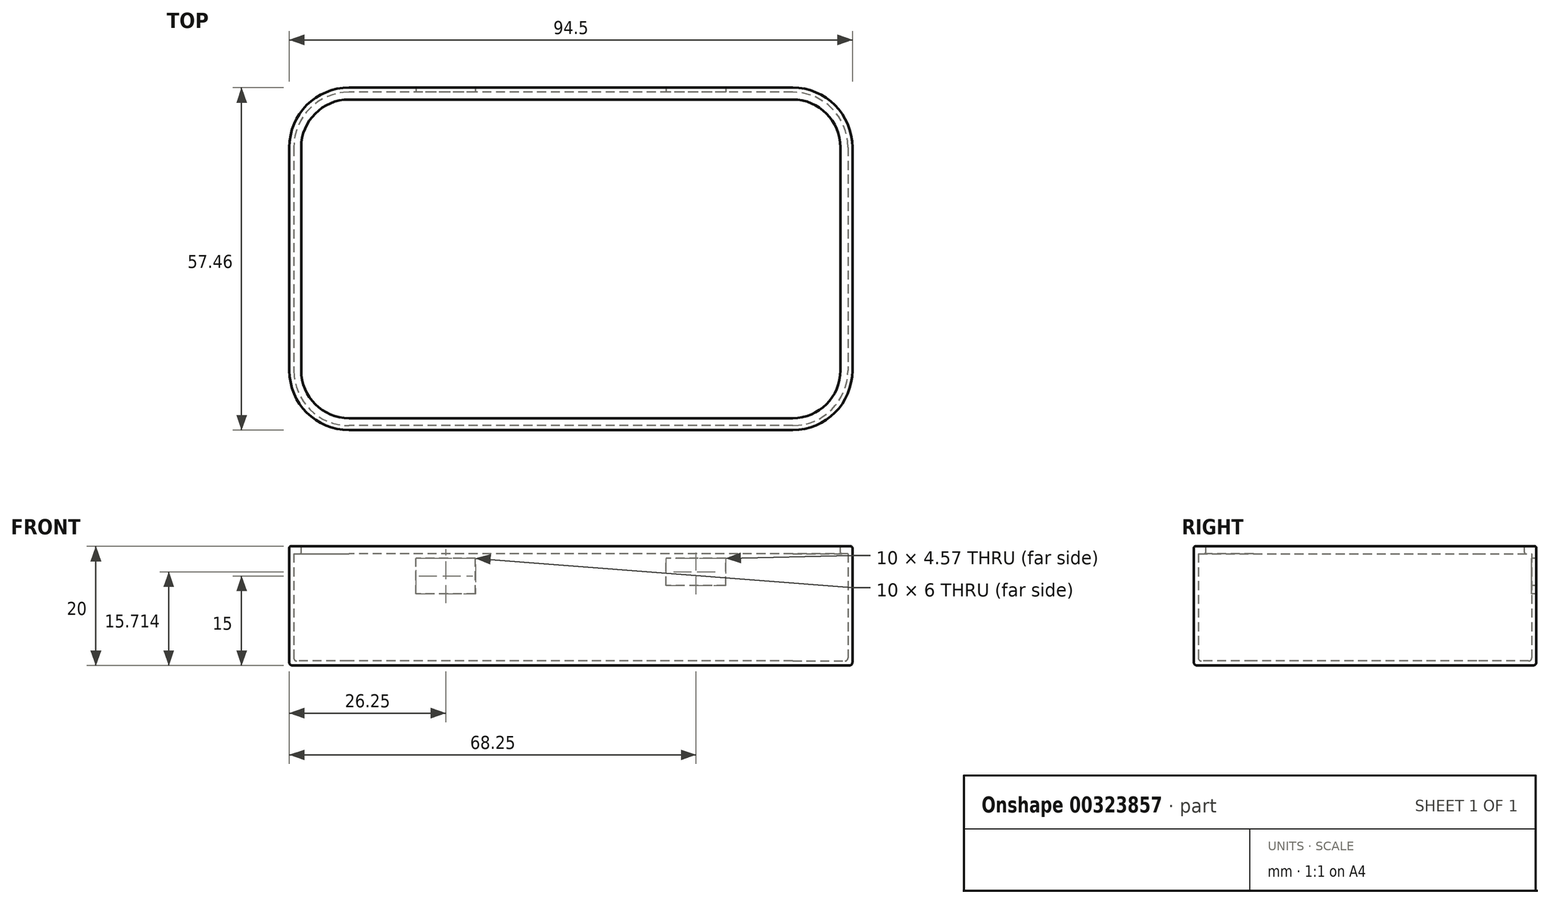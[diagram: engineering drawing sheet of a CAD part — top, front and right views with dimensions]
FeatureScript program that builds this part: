
annotation { "Feature Type Name" : "Feature", "Feature Type Description" : "" }
export const myFeature = defineFeature(function(context is Context, id is Id, definition is map)
    precondition{}
    {
        {
            var Q0;
            Q0=qCreatedBy(makeId("Top.planeOp"),FACE);
            var sketch = newSketch(context, id + "F0", { "sketchPlane" : qUnion([Q0])});
            skLineSegment(sketch, "E0.bottom", {"start": v(37.25, 28.73) * mm, "end": v(-37.25, 28.73) * mm});
            skLineSegment(sketch, "E0.top", {"start": v(37.25, -28.73) * mm, "end": v(-37.25, -28.73) * mm});
            skLineSegment(sketch, "E0.left", {"start": v(47.25, 18.73) * mm, "end": v(47.25, -18.73) * mm});
            skLineSegment(sketch, "E0.right", {"start": v(-47.25, 18.73) * mm, "end": v(-47.25, -18.73) * mm});
            skPoint(sketch, "E0.middle", {"position": v(0, 0) * mm});
            skPoint(sketch, "E1.visualSharp", {"position": v(-47.25, 28.73) * mm});
            skArc(sketch, "E1.filletArc", {"start": v(-37.25, 28.73) * mm, "mid": v(-44.32, 25.8) * mm, "end": v(-47.25, 18.73) * mm});
            skPoint(sketch, "E2.visualSharp", {"position": v(-47.25, -28.73) * mm});
            skArc(sketch, "E2.filletArc", {"start": v(-47.25, -18.73) * mm, "mid": v(-44.32, -25.8) * mm, "end": v(-37.25, -28.73) * mm});
            skPoint(sketch, "E3.visualSharp", {"position": v(47.25, -28.73) * mm});
            skArc(sketch, "E3.filletArc", {"start": v(37.25, -28.73) * mm, "mid": v(44.32, -25.8) * mm, "end": v(47.25, -18.73) * mm});
            skPoint(sketch, "E4.visualSharp", {"position": v(47.25, 28.73) * mm});
            skArc(sketch, "E4.filletArc", {"start": v(47.25, 18.73) * mm, "mid": v(44.32, 25.8) * mm, "end": v(37.25, 28.73) * mm});
            skSolve(sketch);
        }
        {
            var Q0;
            Q0 = qSketchRegion(id + "F0", true);
            extrude(context, id + "F1", {"entities" : qUnion([Q0]), "oppositeDirection" : true, "depth" : 20 * mm});
        }
        {
            var Q0;
            Q0=qCreatedBy(makeId("Top.planeOp"),FACE);
            var sketch = newSketch(context, id + "F2", { "sketchPlane" : qUnion([Q0])});
            skArc(sketch, "E5.0", {"start": v(-45.25, -18.73) * mm, "mid": v(-42.9, -24.38) * mm, "end": v(-37.25, -26.73) * mm});
            skLineSegment(sketch, "E5.1", {"start": v(-45.25, 18.73) * mm, "end": v(-45.25, -18.73) * mm});
            skLineSegment(sketch, "E5.2", {"start": v(-37.25, -26.73) * mm, "end": v(37.25, -26.73) * mm});
            skArc(sketch, "E5.3", {"start": v(-37.25, 26.73) * mm, "mid": v(-42.9, 24.38) * mm, "end": v(-45.25, 18.73) * mm});
            skArc(sketch, "E5.4", {"start": v(37.25, -26.73) * mm, "mid": v(42.9, -24.38) * mm, "end": v(45.25, -18.73) * mm});
            skLineSegment(sketch, "E5.5", {"start": v(45.25, -18.73) * mm, "end": v(45.25, 18.73) * mm});
            skArc(sketch, "E5.6", {"start": v(45.25, 18.73) * mm, "mid": v(42.9, 24.38) * mm, "end": v(37.25, 26.73) * mm});
            skLineSegment(sketch, "E5.7", {"start": v(37.25, 26.73) * mm, "end": v(-37.25, 26.73) * mm});
            skSolve(sketch);
        }
        {
            var Q0;
            Q0 = qSketchRegion(id + "F2", true);
            extrude(context, id + "F3", {"entities" : qUnion([Q0]), "operationType" : NewBodyOperationType.REMOVE, "oppositeDirection" : true, "depth" : 19.25 * mm});
        }
        {
            var Q0;
            Q0=makeQuery(id+"F3.boolean.opBoolean","COPY",FACE,{"derivedFrom":makeQuery(id+"F3.opExtrude","CAP_FACE",FACE,{"disambiguationData":[OSD([sQuery(id+"F2.wireOp",EDGE,"E5.0"),sQuery(id+"F2.wireOp",EDGE,"E5.1"),sQuery(id+"F2.wireOp",EDGE,"E5.2"),sQuery(id+"F2.wireOp",EDGE,"E5.3"),sQuery(id+"F2.wireOp",EDGE,"E5.4"),sQuery(id+"F2.wireOp",EDGE,"E5.5"),sQuery(id+"F2.wireOp",EDGE,"E5.6"),sQuery(id+"F2.wireOp",EDGE,"E5.7")])],"isStart":false})});
            var sketch = newSketch(context, id + "F4", { "sketchPlane" : qUnion([Q0])});
            skLineSegment(sketch, "E6.0", {"start": v(37.25, 27.98) * mm, "end": v(-37.25, 27.98) * mm});
            skArc(sketch, "E6.1", {"start": v(46.5, 18.73) * mm, "mid": v(43.8, 25.27) * mm, "end": v(37.25, 27.98) * mm});
            skArc(sketch, "E6.2", {"start": v(-37.25, 27.98) * mm, "mid": v(-43.8, 25.27) * mm, "end": v(-46.5, 18.73) * mm});
            skLineSegment(sketch, "E6.3", {"start": v(46.5, 18.73) * mm, "end": v(46.5, -18.73) * mm});
            skLineSegment(sketch, "E6.4", {"start": v(-46.5, 18.73) * mm, "end": v(-46.5, -18.73) * mm});
            skArc(sketch, "E6.5", {"start": v(-46.5, -18.73) * mm, "mid": v(-43.8, -25.27) * mm, "end": v(-37.25, -27.98) * mm});
            skLineSegment(sketch, "E6.6", {"start": v(37.25, -27.98) * mm, "end": v(-37.25, -27.98) * mm});
            skArc(sketch, "E6.7", {"start": v(37.25, -27.98) * mm, "mid": v(43.8, -25.27) * mm, "end": v(46.5, -18.73) * mm});
            skSolve(sketch);
        }
        {
            var Q0;
            Q0 = qSketchRegion(id + "F4", true);
            extrude(context, id + "F5", {"entities" : qUnion([Q0]), "operationType" : NewBodyOperationType.REMOVE, "depth" : 18 * mm});
        }
        {
            var Q0;
            Q0=qCreatedBy(makeId("Front.planeOp"),FACE);
            var sketch = newSketch(context, id + "F6", { "sketchPlane" : qUnion([Q0])});
            skPoint(sketch, "E7.endSnap0", {"position": v(0, -19.25) * mm});
            skLineSegment(sketch, "E8.bottom", {"start": v(-16, -8) * mm, "end": v(-26, -8) * mm});
            skLineSegment(sketch, "E8.top", {"start": v(-16, -2) * mm, "end": v(-26, -2) * mm});
            skLineSegment(sketch, "E8.left", {"start": v(-16, -8) * mm, "end": v(-16, -2) * mm});
            skLineSegment(sketch, "E8.right", {"start": v(-26, -8) * mm, "end": v(-26, -2) * mm});
            skPoint(sketch, "E8.middle", {"position": v(-21, -5) * mm});
            skLineSegment(sketch, "E9.bottom", {"start": v(26, -6.57) * mm, "end": v(16, -6.57) * mm});
            skLineSegment(sketch, "E9.top", {"start": v(26, -2) * mm, "end": v(16, -2) * mm});
            skLineSegment(sketch, "E9.left", {"start": v(26, -6.57) * mm, "end": v(26, -2) * mm});
            skLineSegment(sketch, "E9.right", {"start": v(16, -6.57) * mm, "end": v(16, -2) * mm});
            skPoint(sketch, "E9.middle", {"position": v(21, -4.29) * mm});
            skSolve(sketch);
        }
        {
            var Q0;
            Q0 = qSketchRegion(id + "F6", true);
            var Q1;
            Q1=makeQuery(id+"F1.opExtrude","SWEPT_FACE",FACE,{"disambiguationData":[OSD([sQuery(id+"F0.wireOp",EDGE,"E0.bottom")])]});
            extrude(context, id + "F7", {"entities" : qUnion([Q0]), "operationType" : NewBodyOperationType.REMOVE, "endBound" : BoundingType.UP_TO_SURFACE, "oppositeDirection" : true, "endBoundEntityFace" : qUnion([Q1]), "depth" : 25 * mm});
        }
        {
            var Q0;
            Q0=makeQuery(id+"F3.boolean.opBoolean","COPY",EDGE,{"derivedFrom":makeQuery(id+"F3.opExtrude","CAP_EDGE",EDGE,{"disambiguationData":[OSD([sQuery(id+"F2.wireOp",EDGE,"E5.1")])],"isStart":true})});
            var Q1;
            Q1=makeQuery(id+"F1.opExtrude","CAP_EDGE",EDGE,{"disambiguationData":[OSD([sQuery(id+"F0.wireOp",EDGE,"E0.right")])],"isStart":true});
            var Q2;
            Q2=makeQuery(id+"F1.opExtrude","CAP_EDGE",EDGE,{"disambiguationData":[OSD([sQuery(id+"F0.wireOp",EDGE,"E1.filletArc")])],"isStart":true});
            var Q3;
            Q3=makeQuery(id+"F3.boolean.opBoolean","COPY",EDGE,{"derivedFrom":makeQuery(id+"F3.opExtrude","CAP_EDGE",EDGE,{"disambiguationData":[OSD([sQuery(id+"F2.wireOp",EDGE,"E5.3")])],"isStart":true})});
            var Q4;
            Q4=makeQuery(id+"F1.opExtrude","CAP_EDGE",EDGE,{"disambiguationData":[OSD([sQuery(id+"F0.wireOp",EDGE,"E0.bottom")])],"isStart":true});
            var Q5;
            Q5=makeQuery(id+"F3.boolean.opBoolean","COPY",EDGE,{"derivedFrom":makeQuery(id+"F3.opExtrude","CAP_EDGE",EDGE,{"disambiguationData":[OSD([sQuery(id+"F2.wireOp",EDGE,"E5.7")])],"isStart":true})});
            var Q6;
            Q6=makeQuery(id+"F1.opExtrude","CAP_EDGE",EDGE,{"disambiguationData":[OSD([sQuery(id+"F0.wireOp",EDGE,"E4.filletArc")])],"isStart":true});
            var Q7;
            Q7=makeQuery(id+"F3.boolean.opBoolean","COPY",EDGE,{"derivedFrom":makeQuery(id+"F3.opExtrude","CAP_EDGE",EDGE,{"disambiguationData":[OSD([sQuery(id+"F2.wireOp",EDGE,"E5.6")])],"isStart":true})});
            var Q8;
            Q8=makeQuery(id+"F1.opExtrude","CAP_EDGE",EDGE,{"disambiguationData":[OSD([sQuery(id+"F0.wireOp",EDGE,"E0.left")])],"isStart":true});
            var Q9;
            Q9=makeQuery(id+"F3.boolean.opBoolean","COPY",EDGE,{"derivedFrom":makeQuery(id+"F3.opExtrude","CAP_EDGE",EDGE,{"disambiguationData":[OSD([sQuery(id+"F2.wireOp",EDGE,"E5.5")])],"isStart":true})});
            var Q10;
            Q10=makeQuery(id+"F1.opExtrude","CAP_EDGE",EDGE,{"disambiguationData":[OSD([sQuery(id+"F0.wireOp",EDGE,"E3.filletArc")])],"isStart":true});
            var Q11;
            Q11=makeQuery(id+"F3.boolean.opBoolean","COPY",EDGE,{"derivedFrom":makeQuery(id+"F3.opExtrude","CAP_EDGE",EDGE,{"disambiguationData":[OSD([sQuery(id+"F2.wireOp",EDGE,"E5.4")])],"isStart":true})});
            var Q12;
            Q12=makeQuery(id+"F1.opExtrude","CAP_EDGE",EDGE,{"disambiguationData":[OSD([sQuery(id+"F0.wireOp",EDGE,"E0.top")])],"isStart":true});
            var Q13;
            Q13=makeQuery(id+"F3.boolean.opBoolean","COPY",EDGE,{"derivedFrom":makeQuery(id+"F3.opExtrude","CAP_EDGE",EDGE,{"disambiguationData":[OSD([sQuery(id+"F2.wireOp",EDGE,"E5.2")])],"isStart":true})});
            var Q14;
            Q14=makeQuery(id+"F1.opExtrude","CAP_EDGE",EDGE,{"disambiguationData":[OSD([sQuery(id+"F0.wireOp",EDGE,"E2.filletArc")])],"isStart":true});
            var Q15;
            Q15=makeQuery(id+"F3.boolean.opBoolean","COPY",EDGE,{"derivedFrom":makeQuery(id+"F3.opExtrude","CAP_EDGE",EDGE,{"disambiguationData":[OSD([sQuery(id+"F2.wireOp",EDGE,"E5.0")])],"isStart":true})});
            var Q16;
            Q16=makeQuery(id+"F5.boolean.opBoolean","INTERSECT",EDGE,{"derivedFrom":[makeQuery(id+"F3.boolean.opBoolean","COPY",FACE,{"derivedFrom":makeQuery(id+"F3.opExtrude","SWEPT_FACE",FACE,{"disambiguationData":[OSD([sQuery(id+"F2.wireOp",EDGE,"E5.1")])]})}),makeQuery(id+"F5.opExtrude","CAP_FACE",FACE,{"disambiguationData":[OSD([sQuery(id+"F4.wireOp",EDGE,"E6.0"),sQuery(id+"F4.wireOp",EDGE,"E6.1"),sQuery(id+"F4.wireOp",EDGE,"E6.2"),sQuery(id+"F4.wireOp",EDGE,"E6.3"),sQuery(id+"F4.wireOp",EDGE,"E6.4"),sQuery(id+"F4.wireOp",EDGE,"E6.5"),sQuery(id+"F4.wireOp",EDGE,"E6.6"),sQuery(id+"F4.wireOp",EDGE,"E6.7")])],"isStart":false})]});
            var Q17;
            Q17=makeQuery(id+"F5.boolean.opBoolean","INTERSECT",EDGE,{"derivedFrom":[makeQuery(id+"F3.boolean.opBoolean","COPY",FACE,{"derivedFrom":makeQuery(id+"F3.opExtrude","SWEPT_FACE",FACE,{"disambiguationData":[OSD([sQuery(id+"F2.wireOp",EDGE,"E5.3")])]})}),makeQuery(id+"F5.opExtrude","CAP_FACE",FACE,{"disambiguationData":[OSD([sQuery(id+"F4.wireOp",EDGE,"E6.0"),sQuery(id+"F4.wireOp",EDGE,"E6.1"),sQuery(id+"F4.wireOp",EDGE,"E6.2"),sQuery(id+"F4.wireOp",EDGE,"E6.3"),sQuery(id+"F4.wireOp",EDGE,"E6.4"),sQuery(id+"F4.wireOp",EDGE,"E6.5"),sQuery(id+"F4.wireOp",EDGE,"E6.6"),sQuery(id+"F4.wireOp",EDGE,"E6.7")])],"isStart":false})]});
            var Q18;
            Q18=makeQuery(id+"F5.boolean.opBoolean","INTERSECT",EDGE,{"derivedFrom":[makeQuery(id+"F3.boolean.opBoolean","COPY",FACE,{"derivedFrom":makeQuery(id+"F3.opExtrude","SWEPT_FACE",FACE,{"disambiguationData":[OSD([sQuery(id+"F2.wireOp",EDGE,"E5.7")])]})}),makeQuery(id+"F5.opExtrude","CAP_FACE",FACE,{"disambiguationData":[OSD([sQuery(id+"F4.wireOp",EDGE,"E6.0"),sQuery(id+"F4.wireOp",EDGE,"E6.1"),sQuery(id+"F4.wireOp",EDGE,"E6.2"),sQuery(id+"F4.wireOp",EDGE,"E6.3"),sQuery(id+"F4.wireOp",EDGE,"E6.4"),sQuery(id+"F4.wireOp",EDGE,"E6.5"),sQuery(id+"F4.wireOp",EDGE,"E6.6"),sQuery(id+"F4.wireOp",EDGE,"E6.7")])],"isStart":false})]});
            var Q19;
            Q19=makeQuery(id+"F5.boolean.opBoolean","INTERSECT",EDGE,{"derivedFrom":[makeQuery(id+"F3.boolean.opBoolean","COPY",FACE,{"derivedFrom":makeQuery(id+"F3.opExtrude","SWEPT_FACE",FACE,{"disambiguationData":[OSD([sQuery(id+"F2.wireOp",EDGE,"E5.6")])]})}),makeQuery(id+"F5.opExtrude","CAP_FACE",FACE,{"disambiguationData":[OSD([sQuery(id+"F4.wireOp",EDGE,"E6.0"),sQuery(id+"F4.wireOp",EDGE,"E6.1"),sQuery(id+"F4.wireOp",EDGE,"E6.2"),sQuery(id+"F4.wireOp",EDGE,"E6.3"),sQuery(id+"F4.wireOp",EDGE,"E6.4"),sQuery(id+"F4.wireOp",EDGE,"E6.5"),sQuery(id+"F4.wireOp",EDGE,"E6.6"),sQuery(id+"F4.wireOp",EDGE,"E6.7")])],"isStart":false})]});
            var Q20;
            Q20=makeQuery(id+"F5.boolean.opBoolean","INTERSECT",EDGE,{"derivedFrom":[makeQuery(id+"F3.boolean.opBoolean","COPY",FACE,{"derivedFrom":makeQuery(id+"F3.opExtrude","SWEPT_FACE",FACE,{"disambiguationData":[OSD([sQuery(id+"F2.wireOp",EDGE,"E5.5")])]})}),makeQuery(id+"F5.opExtrude","CAP_FACE",FACE,{"disambiguationData":[OSD([sQuery(id+"F4.wireOp",EDGE,"E6.0"),sQuery(id+"F4.wireOp",EDGE,"E6.1"),sQuery(id+"F4.wireOp",EDGE,"E6.2"),sQuery(id+"F4.wireOp",EDGE,"E6.3"),sQuery(id+"F4.wireOp",EDGE,"E6.4"),sQuery(id+"F4.wireOp",EDGE,"E6.5"),sQuery(id+"F4.wireOp",EDGE,"E6.6"),sQuery(id+"F4.wireOp",EDGE,"E6.7")])],"isStart":false})]});
            var Q21;
            Q21=makeQuery(id+"F5.boolean.opBoolean","INTERSECT",EDGE,{"derivedFrom":[makeQuery(id+"F3.boolean.opBoolean","COPY",FACE,{"derivedFrom":makeQuery(id+"F3.opExtrude","SWEPT_FACE",FACE,{"disambiguationData":[OSD([sQuery(id+"F2.wireOp",EDGE,"E5.2")])]})}),makeQuery(id+"F5.opExtrude","CAP_FACE",FACE,{"disambiguationData":[OSD([sQuery(id+"F4.wireOp",EDGE,"E6.0"),sQuery(id+"F4.wireOp",EDGE,"E6.1"),sQuery(id+"F4.wireOp",EDGE,"E6.2"),sQuery(id+"F4.wireOp",EDGE,"E6.3"),sQuery(id+"F4.wireOp",EDGE,"E6.4"),sQuery(id+"F4.wireOp",EDGE,"E6.5"),sQuery(id+"F4.wireOp",EDGE,"E6.6"),sQuery(id+"F4.wireOp",EDGE,"E6.7")])],"isStart":false})]});
            var Q22;
            Q22=makeQuery(id+"F5.boolean.opBoolean","INTERSECT",EDGE,{"derivedFrom":[makeQuery(id+"F3.boolean.opBoolean","COPY",FACE,{"derivedFrom":makeQuery(id+"F3.opExtrude","SWEPT_FACE",FACE,{"disambiguationData":[OSD([sQuery(id+"F2.wireOp",EDGE,"E5.4")])]})}),makeQuery(id+"F5.opExtrude","CAP_FACE",FACE,{"disambiguationData":[OSD([sQuery(id+"F4.wireOp",EDGE,"E6.0"),sQuery(id+"F4.wireOp",EDGE,"E6.1"),sQuery(id+"F4.wireOp",EDGE,"E6.2"),sQuery(id+"F4.wireOp",EDGE,"E6.3"),sQuery(id+"F4.wireOp",EDGE,"E6.4"),sQuery(id+"F4.wireOp",EDGE,"E6.5"),sQuery(id+"F4.wireOp",EDGE,"E6.6"),sQuery(id+"F4.wireOp",EDGE,"E6.7")])],"isStart":false})]});
            var Q23;
            Q23=makeQuery(id+"F5.boolean.opBoolean","INTERSECT",EDGE,{"derivedFrom":[makeQuery(id+"F3.boolean.opBoolean","COPY",FACE,{"derivedFrom":makeQuery(id+"F3.opExtrude","SWEPT_FACE",FACE,{"disambiguationData":[OSD([sQuery(id+"F2.wireOp",EDGE,"E5.0")])]})}),makeQuery(id+"F5.opExtrude","CAP_FACE",FACE,{"disambiguationData":[OSD([sQuery(id+"F4.wireOp",EDGE,"E6.0"),sQuery(id+"F4.wireOp",EDGE,"E6.1"),sQuery(id+"F4.wireOp",EDGE,"E6.2"),sQuery(id+"F4.wireOp",EDGE,"E6.3"),sQuery(id+"F4.wireOp",EDGE,"E6.4"),sQuery(id+"F4.wireOp",EDGE,"E6.5"),sQuery(id+"F4.wireOp",EDGE,"E6.6"),sQuery(id+"F4.wireOp",EDGE,"E6.7")])],"isStart":false})]});
            fillet(context, id + "F8", {"entities" : qUnion([Q0, Q1, Q2, Q3, Q4, Q5, Q6, Q7, Q8, Q9, Q10, Q11, Q12, Q13, Q14, Q15, Q16, Q17, Q18, Q19, Q20, Q21, Q22, Q23]), "radius" : 0.25 * mm, "tangentPropagation" : true, "allowEdgeOverflow" : false});
        }
        {
            var Q0;
            Q0=makeQuery(id+"F1.opExtrude","CAP_EDGE",EDGE,{"disambiguationData":[OSD([sQuery(id+"F0.wireOp",EDGE,"E2.filletArc")])],"isStart":false});
            var Q1;
            Q1=makeQuery(id+"F1.opExtrude","CAP_EDGE",EDGE,{"disambiguationData":[OSD([sQuery(id+"F0.wireOp",EDGE,"E0.top")])],"isStart":false});
            var Q2;
            Q2=makeQuery(id+"F1.opExtrude","CAP_EDGE",EDGE,{"disambiguationData":[OSD([sQuery(id+"F0.wireOp",EDGE,"E0.right")])],"isStart":false});
            var Q3;
            Q3=makeQuery(id+"F1.opExtrude","CAP_EDGE",EDGE,{"disambiguationData":[OSD([sQuery(id+"F0.wireOp",EDGE,"E1.filletArc")])],"isStart":false});
            var Q4;
            Q4=makeQuery(id+"F1.opExtrude","CAP_EDGE",EDGE,{"disambiguationData":[OSD([sQuery(id+"F0.wireOp",EDGE,"E0.bottom")])],"isStart":false});
            var Q5;
            Q5=makeQuery(id+"F1.opExtrude","CAP_EDGE",EDGE,{"disambiguationData":[OSD([sQuery(id+"F0.wireOp",EDGE,"E4.filletArc")])],"isStart":false});
            var Q6;
            Q6=makeQuery(id+"F1.opExtrude","CAP_EDGE",EDGE,{"disambiguationData":[OSD([sQuery(id+"F0.wireOp",EDGE,"E0.left")])],"isStart":false});
            var Q7;
            Q7=makeQuery(id+"F1.opExtrude","CAP_EDGE",EDGE,{"disambiguationData":[OSD([sQuery(id+"F0.wireOp",EDGE,"E3.filletArc")])],"isStart":false});
            var Q8;
            Q8=makeQuery(id+"F5.boolean.opBoolean","COPY",EDGE,{"derivedFrom":makeQuery(id+"F5.opExtrude","CAP_EDGE",EDGE,{"disambiguationData":[OSD([sQuery(id+"F4.wireOp",EDGE,"E6.4")])],"isStart":true})});
            var Q9;
            Q9=makeQuery(id+"F5.boolean.opBoolean","COPY",EDGE,{"derivedFrom":makeQuery(id+"F5.opExtrude","CAP_EDGE",EDGE,{"disambiguationData":[OSD([sQuery(id+"F4.wireOp",EDGE,"E6.2")])],"isStart":true})});
            var Q10;
            Q10=makeQuery(id+"F5.boolean.opBoolean","COPY",EDGE,{"derivedFrom":makeQuery(id+"F5.opExtrude","CAP_EDGE",EDGE,{"disambiguationData":[OSD([sQuery(id+"F4.wireOp",EDGE,"E6.0")])],"isStart":true})});
            var Q11;
            Q11=makeQuery(id+"F5.boolean.opBoolean","COPY",EDGE,{"derivedFrom":makeQuery(id+"F5.opExtrude","CAP_EDGE",EDGE,{"disambiguationData":[OSD([sQuery(id+"F4.wireOp",EDGE,"E6.1")])],"isStart":true})});
            var Q12;
            Q12=makeQuery(id+"F5.boolean.opBoolean","COPY",EDGE,{"derivedFrom":makeQuery(id+"F5.opExtrude","CAP_EDGE",EDGE,{"disambiguationData":[OSD([sQuery(id+"F4.wireOp",EDGE,"E6.3")])],"isStart":true})});
            var Q13;
            Q13=makeQuery(id+"F5.boolean.opBoolean","COPY",EDGE,{"derivedFrom":makeQuery(id+"F5.opExtrude","CAP_EDGE",EDGE,{"disambiguationData":[OSD([sQuery(id+"F4.wireOp",EDGE,"E6.7")])],"isStart":true})});
            var Q14;
            Q14=makeQuery(id+"F5.boolean.opBoolean","COPY",EDGE,{"derivedFrom":makeQuery(id+"F5.opExtrude","CAP_EDGE",EDGE,{"disambiguationData":[OSD([sQuery(id+"F4.wireOp",EDGE,"E6.6")])],"isStart":true})});
            var Q15;
            Q15=makeQuery(id+"F5.boolean.opBoolean","COPY",EDGE,{"derivedFrom":makeQuery(id+"F5.opExtrude","CAP_EDGE",EDGE,{"disambiguationData":[OSD([sQuery(id+"F4.wireOp",EDGE,"E6.5")])],"isStart":true})});
            fillet(context, id + "F9", {"entities" : qUnion([Q0, Q1, Q2, Q3, Q4, Q5, Q6, Q7, Q8, Q9, Q10, Q11, Q12, Q13, Q14, Q15]), "radius" : 0.5 * mm, "tangentPropagation" : true, "allowEdgeOverflow" : false});
        }
    });
